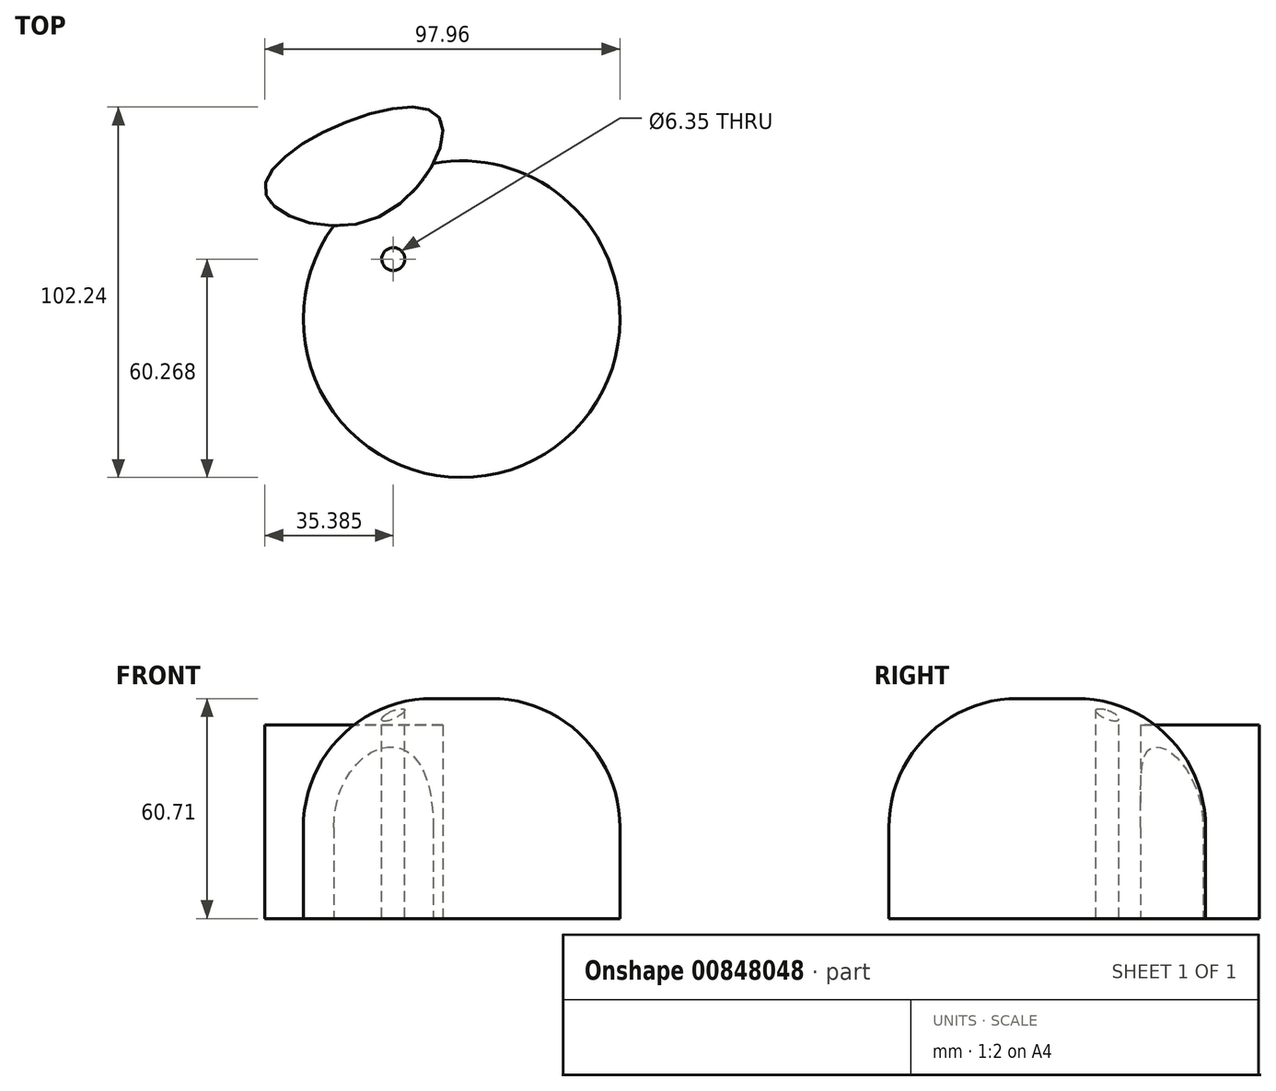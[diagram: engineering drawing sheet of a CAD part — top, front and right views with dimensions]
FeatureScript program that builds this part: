
annotation { "Feature Type Name" : "Feature", "Feature Type Description" : "" }
export const myFeature = defineFeature(function(context is Context, id is Id, definition is map)
    precondition{}
    {
        {
            var Q0;
            Q0=qCreatedBy(makeId("Top.planeOp"),FACE);
            var sketch = newSketch(context, id + "F0", { "sketchPlane" : qUnion([Q0])});
            skCircle(sketch, "E0", {"center": v(0, 0) * mm, "radius": 43.7 * mm});
            skSolve(sketch);
        }
        {
            var Q0;
            Q0=makeQuery(id+"F0.imprint","IMPRINT",FACE,{"disambiguationData":[TD([[makeQuery(id+"F0.imprint","IMPRINT",EDGE,{"derivedFrom":sQuery(id+"F0.wireOp",EDGE,"E0")}),1.0]])]});
            extrude(context, id + "F1", {"entities" : qUnion([Q0]), "depth" : 60.7 * mm, "offsetDistance" : 25.4 * mm});
        }
        {
            var Q0;
            Q0=makeQuery(id+"F1.opExtrude","CAP_FACE",FACE,{"disambiguationData":[OSD([sQuery(id+"F0.wireOp",EDGE,"E0")])],"isStart":false});
            var sketch = newSketch(context, id + "F2", { "sketchPlane" : qUnion([Q0])});
            skCircle(sketch, "E1", {"center": v(-18.88, 16.57) * mm, "radius": 8.16 * mm});
            skSolve(sketch);
        }
        {
            var Q0;
            Q0=sQuery(id+"F2.wireOp",VERTEX,"E1.center");
            var Q1;
            Q1=makeQuery(id+"F1.opExtrude","SWEPT_BODY",BODY,{"disambiguationData":[OSD([sQuery(id+"F0.wireOp",EDGE,"E0")])]});
            hole(context, id + "F3", {"style" : HoleStyle.SIMPLE, "endStyle" : HoleEndStyle.THROUGH, "holeDiameter" : 6.35 * mm, "majorDiameter" : 6.35 * mm, "isTappedThrough" : true, "tappedDepth" : 12.7 * mm, "tapClearance" : 3, "locations" : qUnion([Q0]), "scope" : qUnion([Q1])});
        }
        {
            var Q0;
            Q0=makeQuery(id+"F1.opExtrude","CAP_EDGE",EDGE,{"disambiguationData":[OSD([sQuery(id+"F0.wireOp",EDGE,"E0")])],"isStart":false});
            fillet(context, id + "F4", {"entities" : qUnion([Q0]), "radius" : 35.57 * mm, "tangentPropagation" : true, "allowEdgeOverflow" : false});
        }
        {
            var Q0;
            Q0=qCreatedBy(makeId("Top.planeOp"),FACE);
            var sketch = newSketch(context, id + "F5", { "sketchPlane" : qUnion([Q0])});
            skFitSpline(sketch, "E2", {"points": [v(-53.93, 34.25) * mm, v(-36.19, 52.55) * mm, v(-5.96, 55.32) * mm, v(-23.7, 27.87) * mm, v(-53.93, 34.25) * mm]});
            skSolve(sketch);
        }
        {
            var Q0;
            Q0 = qSketchRegion(id + "F5", true);
            extrude(context, id + "F6", {"entities" : qUnion([Q0]), "operationType" : NewBodyOperationType.ADD, "depth" : 53.4 * mm, "offsetDistance" : 25 * mm});
        }
    });
